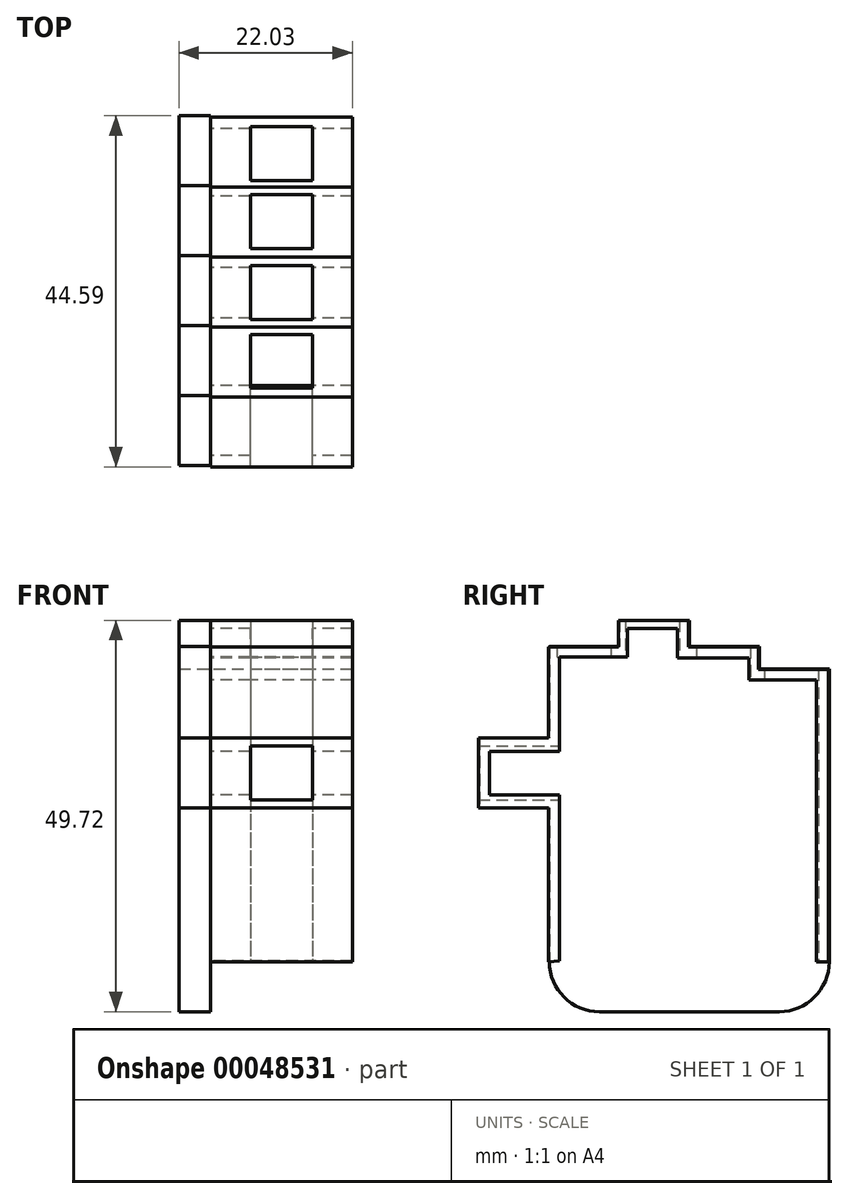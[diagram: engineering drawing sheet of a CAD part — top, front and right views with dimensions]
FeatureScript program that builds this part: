
annotation { "Feature Type Name" : "Feature", "Feature Type Description" : "" }
export const myFeature = defineFeature(function(context is Context, id is Id, definition is map)
    precondition{}
    {
        {
            var Q0;
            Q0=qCreatedBy(makeId("Right.planeOp"),FACE);
            var sketch = newSketch(context, id + "F0", { "sketchPlane" : qUnion([Q0])});
            skLineSegment(sketch, "E0.bottom", {"start": v(-26.9, 23.27) * mm, "end": v(-18.01, 23.27) * mm});
            skLineSegment(sketch, "E0.top", {"start": v(-26.9, 11.7) * mm, "end": v(-18.01, 11.7) * mm});
            skLineSegment(sketch, "E0.left", {"start": v(-26.9, 23.27) * mm, "end": v(-26.9, 11.7) * mm});
            skLineSegment(sketch, "E0.right", {"start": v(-18.01, 23.27) * mm, "end": v(-18.01, 11.7) * mm});
            skLineSegment(sketch, "E1.bottom", {"start": v(-18.01, 26.63) * mm, "end": v(-9.12, 26.63) * mm});
            skLineSegment(sketch, "E1.top", {"start": v(-18.01, 11.7) * mm, "end": v(-9.12, 11.7) * mm});
            skLineSegment(sketch, "E1.left", {"start": v(-18.01, 26.63) * mm, "end": v(-18.01, 11.7) * mm});
            skLineSegment(sketch, "E1.right", {"start": v(-9.12, 26.63) * mm, "end": v(-9.12, 11.7) * mm});
            skLineSegment(sketch, "E2.right", {"start": v(-9.12, 23.27) * mm, "end": v(-9.12, 23.27) * mm});
            skLineSegment(sketch, "E3.bottom", {"start": v(-9.12, 23.27) * mm, "end": v(-0.23, 23.27) * mm});
            skLineSegment(sketch, "E3.top", {"start": v(-9.12, 11.7) * mm, "end": v(-0.23, 11.7) * mm});
            skLineSegment(sketch, "E3.left", {"start": v(-9.12, 23.27) * mm, "end": v(-9.12, 11.7) * mm});
            skLineSegment(sketch, "E3.right", {"start": v(-0.23, 23.27) * mm, "end": v(-0.23, 11.7) * mm});
            skLineSegment(sketch, "E4.bottom", {"start": v(-0.23, 20.42) * mm, "end": v(8.66, 20.42) * mm});
            skLineSegment(sketch, "E4.top", {"start": v(-0.23, 11.7) * mm, "end": v(8.66, 11.7) * mm});
            skLineSegment(sketch, "E4.left", {"start": v(-0.23, 20.42) * mm, "end": v(-0.23, 11.7) * mm});
            skLineSegment(sketch, "E4.right", {"start": v(8.66, 20.42) * mm, "end": v(8.66, 11.7) * mm});
            skLineSegment(sketch, "E5.bottom", {"start": v(-26.9, 11.7) * mm, "end": v(-35.8, 11.7) * mm});
            skLineSegment(sketch, "E5.top", {"start": v(-26.9, 2.81) * mm, "end": v(-35.8, 2.81) * mm});
            skLineSegment(sketch, "E5.left", {"start": v(-26.9, 11.7) * mm, "end": v(-26.9, 2.81) * mm});
            skLineSegment(sketch, "E5.right", {"start": v(-35.8, 11.7) * mm, "end": v(-35.8, 2.81) * mm});
            skLineSegment(sketch, "E6.bottom", {"start": v(-26.9, 11.7) * mm, "end": v(8.66, 11.7) * mm});
            skLineSegment(sketch, "E6.top", {"start": v(-26.9, 2.84) * mm, "end": v(8.66, 2.84) * mm});
            skLineSegment(sketch, "E6.left", {"start": v(-26.9, 11.7) * mm, "end": v(-26.9, 2.84) * mm});
            skLineSegment(sketch, "E6.right", {"start": v(8.66, 11.7) * mm, "end": v(8.66, 2.84) * mm});
            skLineSegment(sketch, "E7.bottom", {"start": v(-26.9, 2.84) * mm, "end": v(8.64, 2.84) * mm});
            skLineSegment(sketch, "E7.top", {"start": v(-20.55, -23.1) * mm, "end": v(2.3, -23.1) * mm});
            skLineSegment(sketch, "E7.left", {"start": v(-26.9, 2.84) * mm, "end": v(-26.9, -16.74) * mm});
            skLineSegment(sketch, "E7.right", {"start": v(8.64, 2.84) * mm, "end": v(8.64, -16.74) * mm});
            skPoint(sketch, "E8.visualSharp", {"position": v(8.64, -23.1) * mm});
            skArc(sketch, "E8.filletArc", {"start": v(2.3, -23.1) * mm, "mid": v(6.78, -21.23) * mm, "end": v(8.64, -16.74) * mm});
            skPoint(sketch, "E9.visualSharp", {"position": v(-26.9, -23.1) * mm});
            skArc(sketch, "E9.filletArc", {"start": v(-26.9, -16.74) * mm, "mid": v(-25.04, -21.23) * mm, "end": v(-20.55, -23.1) * mm});
            skSolve(sketch);
        }
        {
            var Q0;
            Q0 = qSketchRegion(id + "F0", true);
            extrude(context, id + "F1", {"entities" : qUnion([Q0]), "oppositeDirection" : true, "depth" : 4 * mm});
        }
        {
            var Q0;
            Q0=qCreatedBy(makeId("Right.planeOp"),FACE);
            var sketch = newSketch(context, id + "F2", { "sketchPlane" : qUnion([Q0])});
            skLineSegment(sketch, "E10.bottom", {"start": v(-27.04, 23.26) * mm, "end": v(-18.15, 23.26) * mm});
            skLineSegment(sketch, "E10.left", {"start": v(-27.04, 23.26) * mm, "end": v(-27.04, 11.69) * mm});
            skLineSegment(sketch, "E11.bottom", {"start": v(-18.15, 26.61) * mm, "end": v(-9.26, 26.61) * mm});
            skLineSegment(sketch, "E11.left", {"start": v(-18.15, 26.61) * mm, "end": v(-18.15, 23.26) * mm});
            skLineSegment(sketch, "E11.right", {"start": v(-9.26, 26.61) * mm, "end": v(-9.26, 23.26) * mm});
            skLineSegment(sketch, "E12.right", {"start": v(-9.26, 23.26) * mm, "end": v(-9.26, 23.26) * mm});
            skLineSegment(sketch, "E13.bottom", {"start": v(-9.26, 23.26) * mm, "end": v(-0.37, 23.26) * mm});
            skLineSegment(sketch, "E13.right", {"start": v(-0.37, 23.26) * mm, "end": v(-0.37, 20.4) * mm});
            skLineSegment(sketch, "E14.bottom", {"start": v(-0.37, 20.4) * mm, "end": v(8.52, 20.4) * mm});
            skLineSegment(sketch, "E14.right", {"start": v(8.52, 20.4) * mm, "end": v(8.52, 11.69) * mm});
            skLineSegment(sketch, "E15.bottom", {"start": v(-27.04, 11.69) * mm, "end": v(-35.93, 11.69) * mm});
            skLineSegment(sketch, "E15.top", {"start": v(-27.04, 2.8) * mm, "end": v(-35.93, 2.8) * mm});
            skLineSegment(sketch, "E15.right", {"start": v(-35.93, 11.69) * mm, "end": v(-35.93, 2.8) * mm});
            skLineSegment(sketch, "E16.right", {"start": v(8.52, 11.69) * mm, "end": v(8.52, -4.87) * mm});
            skLineSegment(sketch, "E17.left", {"start": v(-27.04, -4.87) * mm, "end": v(-27.04, -16.78) * mm});
            skLineSegment(sketch, "E17.right", {"start": v(8.52, -4.87) * mm, "end": v(8.52, -16.78) * mm});
            skPoint(sketch, "E18.visualSharp", {"position": v(8.52, -23.13) * mm});
            skPoint(sketch, "E19.visualSharp", {"position": v(-27.04, -23.13) * mm});
            skLineSegment(sketch, "E20", {"start": v(-34.51, 10) * mm, "end": v(-34.51, 4.44) * mm});
            skLineSegment(sketch, "E21", {"start": v(-34.51, 4.44) * mm, "end": v(-25.64, 4.44) * mm});
            skLineSegment(sketch, "E22", {"start": v(-25.64, 4.44) * mm, "end": v(-25.64, -16.66) * mm});
            skLineSegment(sketch, "E23", {"start": v(-34.51, 10) * mm, "end": v(-25.64, 10) * mm});
            skLineSegment(sketch, "E24", {"start": v(-25.64, 10) * mm, "end": v(-25.64, 21.97) * mm});
            skLineSegment(sketch, "E25", {"start": v(-25.64, 21.97) * mm, "end": v(-17, 21.97) * mm});
            skLineSegment(sketch, "E26", {"start": v(-17, 21.97) * mm, "end": v(-17, 25.59) * mm});
            skLineSegment(sketch, "E27", {"start": v(-17, 25.59) * mm, "end": v(-10.6, 25.59) * mm});
            skLineSegment(sketch, "E28", {"start": v(-10.6, 25.59) * mm, "end": v(-10.6, 21.83) * mm});
            skLineSegment(sketch, "E29", {"start": v(-10.6, 21.83) * mm, "end": v(-1.55, 21.83) * mm});
            skLineSegment(sketch, "E30", {"start": v(-1.55, 21.83) * mm, "end": v(-1.55, 19.05) * mm});
            skLineSegment(sketch, "E31", {"start": v(-1.55, 19.05) * mm, "end": v(7.02, 19.05) * mm});
            skLineSegment(sketch, "E32", {"start": v(7.02, 19.05) * mm, "end": v(7.02, -16.78) * mm});
            skLineSegment(sketch, "E33", {"start": v(-27.04, -16.78) * mm, "end": v(-25.64, -16.66) * mm});
            skLineSegment(sketch, "E34", {"start": v(7.02, -16.78) * mm, "end": v(8.52, -16.78) * mm});
            skPoint(sketch, "E35.orphan", {"position": v(-18.15, 11.69) * mm});
            skPoint(sketch, "E36.orphan", {"position": v(-9.26, 11.69) * mm});
            skLineSegment(sketch, "E37.trimOffspring", {"start": v(-27.04, 2.8) * mm, "end": v(-27.04, -4.87) * mm});
            skSolve(sketch);
        }
        {
            var Q0;
            Q0 = qSketchRegion(id + "F2", true);
            extrude(context, id + "F3", {"entities" : qUnion([Q0]), "operationType" : NewBodyOperationType.ADD, "depth" : 18.03 * mm});
        }
        {
            var Q0;
            Q0=qCreatedBy(makeId("Right.planeOp"),FACE);
            var sketch = newSketch(context, id + "F4", { "sketchPlane" : qUnion([Q0])});
            skLineSegment(sketch, "E38.bottom", {"start": v(-25.94, 23.26) * mm, "end": v(-19.1, 23.26) * mm});
            skLineSegment(sketch, "E38.top", {"start": v(-25.94, 21.97) * mm, "end": v(-19.1, 21.97) * mm});
            skLineSegment(sketch, "E38.left", {"start": v(-25.94, 23.26) * mm, "end": v(-25.94, 21.97) * mm});
            skLineSegment(sketch, "E38.right", {"start": v(-19.1, 23.26) * mm, "end": v(-19.1, 21.97) * mm});
            skLineSegment(sketch, "E39.bottom", {"start": v(-17.22, 20.96) * mm, "end": v(-10.38, 20.96) * mm});
            skLineSegment(sketch, "E39.top", {"start": v(-17.22, 26.66) * mm, "end": v(-10.38, 26.66) * mm});
            skLineSegment(sketch, "E39.left", {"start": v(-17.22, 26.66) * mm, "end": v(-17.22, 20.96) * mm});
            skLineSegment(sketch, "E39.right", {"start": v(-10.38, 26.66) * mm, "end": v(-10.38, 20.96) * mm});
            skLineSegment(sketch, "E40.bottom", {"start": v(-8.21, 18.35) * mm, "end": v(-1.37, 18.35) * mm});
            skLineSegment(sketch, "E40.top", {"start": v(-8.21, 23.42) * mm, "end": v(-1.37, 23.42) * mm});
            skLineSegment(sketch, "E40.left", {"start": v(-8.21, 23.42) * mm, "end": v(-8.21, 18.35) * mm});
            skLineSegment(sketch, "E40.right", {"start": v(-1.37, 23.42) * mm, "end": v(-1.37, 18.35) * mm});
            skLineSegment(sketch, "E41.bottom", {"start": v(0.44, -17.19) * mm, "end": v(7.28, -17.19) * mm});
            skLineSegment(sketch, "E41.top", {"start": v(0.44, 20.43) * mm, "end": v(7.28, 20.43) * mm});
            skLineSegment(sketch, "E41.left", {"start": v(0.44, 20.43) * mm, "end": v(0.44, -17.19) * mm});
            skLineSegment(sketch, "E41.right", {"start": v(7.28, 20.43) * mm, "end": v(7.28, -17.19) * mm});
            skLineSegment(sketch, "E42.bottom", {"start": v(-35.94, 10.65) * mm, "end": v(-24.87, 10.65) * mm});
            skLineSegment(sketch, "E42.top", {"start": v(-35.94, 3.8) * mm, "end": v(-24.87, 3.8) * mm});
            skLineSegment(sketch, "E42.left", {"start": v(-24.87, 10.65) * mm, "end": v(-24.87, 3.8) * mm});
            skLineSegment(sketch, "E42.right", {"start": v(-35.94, 10.65) * mm, "end": v(-35.94, 3.8) * mm});
            skSolve(sketch);
        }
        {
            var Q0;
            Q0 = qSketchRegion(id + "F4", true);
            extrude(context, id + "F5", {"entities" : qUnion([Q0]), "operationType" : NewBodyOperationType.REMOVE, "depth" : 12.95 * mm, "hasSecondDirection" : true, "secondDirectionOppositeDirection" : false, "secondDirectionDepth" : 5.08 * mm});
        }
    });
